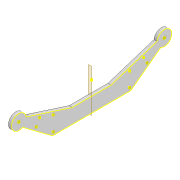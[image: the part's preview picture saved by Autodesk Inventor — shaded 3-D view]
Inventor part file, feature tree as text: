
AUTODESK INVENTOR PART (.ipt)
format: ipt  version: 2022 (Build 260153000, 153)  size: 254,976 bytes
history: native  units: mm
features: sketch x2, extrude x1, projected_geometry x1
ambient origin geometry x8: Origin, YZ Plane, XZ Plane, XY Plane, X Axis, Y Axis, Z Axis, Center Point
bodies: Solid1 (feature_tree)
feature tree (4):
  extrude  "Extrusion1"  Depth=3.9mm
  sketch  "Sketch8"  dims[d6=5.0mm d7=0.0mm d25=3.0mm d28=3.0mm d43=59.0mm d44=65.0mm d45=65.0mm d47=59.0mm d48=10.0mm d49=10.0mm d50=10.0mm d52=14.0mm d53=3.0mm d54=3.0mm d55=4.0mm d56=4.0mm d57=25.0mm d58=25.0mm d59=10.0mm d60=10.0mm d61=10.0mm d62=3.0mm d63=3.0mm d64=3.0mm d65=3.0mm d66=3.0mm d67=10.0mm d68=25.0mm d69=3.0mm d70=3.0mm d71=10.0mm d72=25.0mm d73=25.0mm d74=25.0mm d76=3.0mm d78=3.0mm d79=3.0mm d80=3.0mm d81=6.0mm d82=6.0mm d83=2.0mm]
  sketch  "Sketch1"  dims[d2=3.9mm d4=3.9mm]
  projected_geometry  "Project Cut Edges1"
